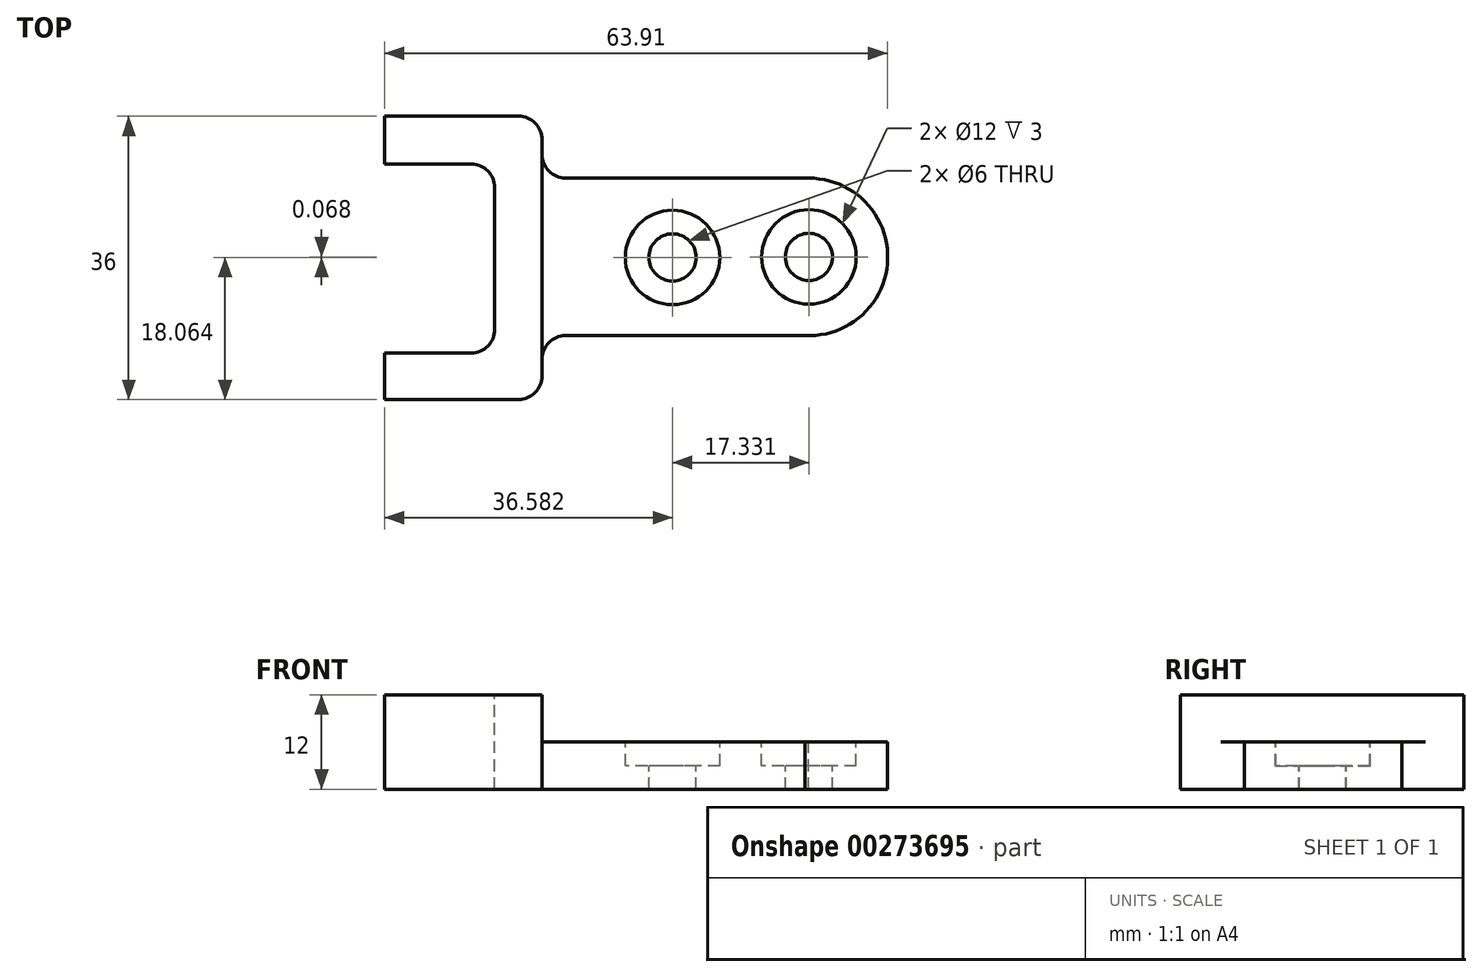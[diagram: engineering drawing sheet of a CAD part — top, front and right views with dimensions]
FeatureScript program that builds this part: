
annotation { "Feature Type Name" : "Feature", "Feature Type Description" : "" }
export const myFeature = defineFeature(function(context is Context, id is Id, definition is map)
    precondition{}
    {
        {
            var Q0;
            Q0=qCreatedBy(makeId("Top.planeOp"),FACE);
            var sketch = newSketch(context, id + "F0", { "sketchPlane" : qUnion([Q0])});
            skLineSegment(sketch, "E0.bottom", {"start": v(-60.7, 27.41) * mm, "end": v(-40.7, 27.41) * mm});
            skLineSegment(sketch, "E0.top", {"start": v(-60.7, -8.59) * mm, "end": v(-40.7, -8.59) * mm});
            skLineSegment(sketch, "E0.left", {"start": v(-60.7, 27.41) * mm, "end": v(-60.7, -8.59) * mm});
            skLineSegment(sketch, "E0.right", {"start": v(-40.7, 27.41) * mm, "end": v(-40.7, -8.59) * mm});
            skSolve(sketch);
        }
        {
            var Q0;
            Q0=makeQuery(id+"F0.imprint","IMPRINT",FACE,{"disambiguationData":[TD([[makeQuery(id+"F0.imprint","IMPRINT",EDGE,{"derivedFrom":sQuery(id+"F0.wireOp",EDGE,"E0.bottom")}),-1.0]])]});
            extrude(context, id + "F1", {"entities" : qUnion([Q0]), "depth" : 12 * mm});
        }
        {
            var Q0;
            Q0=makeQuery(id+"F1.opExtrude","CAP_FACE",FACE,{"disambiguationData":[OSD([sQuery(id+"F0.wireOp",EDGE,"E0.bottom"),sQuery(id+"F0.wireOp",EDGE,"E0.top"),sQuery(id+"F0.wireOp",EDGE,"E0.left"),sQuery(id+"F0.wireOp",EDGE,"E0.right")])],"isStart":false});
            var sketch = newSketch(context, id + "F2", { "sketchPlane" : qUnion([Q0])});
            skLineSegment(sketch, "E1.bottom", {"start": v(-46.7, -2.66) * mm, "end": v(-60.7, -2.66) * mm});
            skLineSegment(sketch, "E1.top", {"start": v(-46.7, 21.34) * mm, "end": v(-60.7, 21.34) * mm});
            skLineSegment(sketch, "E1.left", {"start": v(-46.7, -2.66) * mm, "end": v(-46.7, 21.34) * mm});
            skLineSegment(sketch, "E1.right", {"start": v(-60.7, -2.66) * mm, "end": v(-60.7, 21.34) * mm});
            skSolve(sketch);
        }
        {
            var Q0;
            Q0=makeQuery(id+"F2.imprint","IMPRINT",FACE,{"disambiguationData":[TD([[makeQuery(id+"F2.imprint","IMPRINT",EDGE,{"derivedFrom":sQuery(id+"F2.wireOp",EDGE,"E1.bottom")}),-1.0]])]});
            extrude(context, id + "F3", {"entities" : qUnion([Q0]), "operationType" : NewBodyOperationType.REMOVE, "oppositeDirection" : true, "depth" : 25 * mm});
        }
        {
            var Q0;
            Q0=makeQuery(id+"F1.opExtrude","SWEPT_EDGE",EDGE,{"disambiguationData":[OSD([sQuery(id+"F0.wireOp",EDGE,"E0.top"),sQuery(id+"F0.wireOp",EDGE,"E0.right")])]});
            fillet(context, id + "F4", {"entities" : qUnion([Q0]), "radius" : 3 * mm, "tangentPropagation" : true, "allowEdgeOverflow" : false});
        }
        {
            var Q0;
            Q0=makeQuery(id+"F1.opExtrude","SWEPT_EDGE",EDGE,{"disambiguationData":[OSD([sQuery(id+"F0.wireOp",EDGE,"E0.bottom"),sQuery(id+"F0.wireOp",EDGE,"E0.right")])]});
            var Q1;
            Q1=makeQuery(id+"F3.boolean.opBoolean","COPY",EDGE,{"derivedFrom":makeQuery(id+"F3.opExtrude","SWEPT_EDGE",EDGE,{"disambiguationData":[OSD([sQuery(id+"F2.wireOp",EDGE,"E1.bottom"),sQuery(id+"F2.wireOp",EDGE,"E1.left")])]})});
            var Q2;
            Q2=makeQuery(id+"F3.boolean.opBoolean","COPY",EDGE,{"derivedFrom":makeQuery(id+"F3.opExtrude","SWEPT_EDGE",EDGE,{"disambiguationData":[OSD([sQuery(id+"F2.wireOp",EDGE,"E1.top"),sQuery(id+"F2.wireOp",EDGE,"E1.left")])]})});
            fillet(context, id + "F5", {"entities" : qUnion([Q0, Q1, Q2]), "radius" : 3 * mm, "tangentPropagation" : true, "allowEdgeOverflow" : false});
        }
        {
            var Q0;
            Q0=qCreatedBy(makeId("Top.planeOp"),FACE);
            var sketch = newSketch(context, id + "F6", { "sketchPlane" : qUnion([Q0])});
            skLineSegment(sketch, "E2.bottom", {"start": v(-40.85, -0.44) * mm, "end": v(-6.85, -0.44) * mm});
            skLineSegment(sketch, "E2.top", {"start": v(-40.85, 19.56) * mm, "end": v(-6.85, 19.56) * mm});
            skLineSegment(sketch, "E2.left", {"start": v(-40.85, -0.44) * mm, "end": v(-40.85, 19.56) * mm});
            skLineSegment(sketch, "E2.right", {"start": v(-6.85, -0.44) * mm, "end": v(-6.85, 19.56) * mm});
            skSolve(sketch);
        }
        {
            var Q0;
            Q0=makeQuery(id+"F6.imprint","IMPRINT",FACE,{"disambiguationData":[TD([[makeQuery(id+"F6.imprint","IMPRINT",EDGE,{"derivedFrom":sQuery(id+"F6.wireOp",EDGE,"E2.bottom")}),1.0]])]});
            extrude(context, id + "F7", {"entities" : qUnion([Q0]), "operationType" : NewBodyOperationType.ADD, "depth" : 6 * mm});
        }
        {
            var Q0;
            Q0=makeQuery(id+"F7.boolean.opBoolean","INTERSECT",EDGE,{"derivedFrom":[makeQuery(id+"F1.opExtrude","SWEPT_FACE",FACE,{"disambiguationData":[OSD([sQuery(id+"F0.wireOp",EDGE,"E0.right")])]}),makeQuery(id+"F7.opExtrude","SWEPT_FACE",FACE,{"disambiguationData":[OSD([sQuery(id+"F6.wireOp",EDGE,"E2.top")])]})]});
            fillet(context, id + "F8", {"entities" : qUnion([Q0]), "radius" : 3 * mm, "tangentPropagation" : true, "allowEdgeOverflow" : false});
        }
        {
            var Q0;
            Q0=makeQuery(id+"F7.boolean.opBoolean","INTERSECT",EDGE,{"derivedFrom":[makeQuery(id+"F1.opExtrude","SWEPT_FACE",FACE,{"disambiguationData":[OSD([sQuery(id+"F0.wireOp",EDGE,"E0.right")])]}),makeQuery(id+"F7.opExtrude","SWEPT_FACE",FACE,{"disambiguationData":[OSD([sQuery(id+"F6.wireOp",EDGE,"E2.bottom")])]})]});
            fillet(context, id + "F9", {"entities" : qUnion([Q0]), "radius" : 3 * mm, "tangentPropagation" : true, "allowEdgeOverflow" : false});
        }
        {
            var Q0;
            Q0=makeQuery(id+"F7.opExtrude","CAP_FACE",FACE,{"disambiguationData":[OSD([sQuery(id+"F6.wireOp",EDGE,"E2.bottom"),sQuery(id+"F6.wireOp",EDGE,"E2.top"),sQuery(id+"F6.wireOp",EDGE,"E2.left"),sQuery(id+"F6.wireOp",EDGE,"E2.right")])],"isStart":false});
            var sketch = newSketch(context, id + "F10", { "sketchPlane" : qUnion([Q0])});
            skLineSegment(sketch, "E3", {"start": v(-6.85, 19.56) * mm, "end": v(-6.85, 9.56) * mm});
            skSolve(sketch);
        }
        {
            var Q0;
            {var subQ8=sQuery(id+"F10.wireOp",EDGE,"E3");Q0=makeQuery(id+"F10.imprint","IMPRINT",FACE,{"disambiguationData":[TD([[makeQuery(id+"F10.imprint","IMPRINT",EDGE,{"derivedFrom":subQ8}),1.0]])]});}
            var sketch = newSketch(context, id + "F11", { "sketchPlane" : qUnion([Q0])});
            skCircle(sketch, "E4", {"center": v(-6.8, 9.54) * mm, "radius": 10 * mm});
            skSolve(sketch);
        }
        {
            var Q0;
            {var subQ0=sQuery(id+"F11.wireOp",EDGE,"E4");var subQ1=sQuery(id+"F10.wireOp",EDGE,"E3");var subQ2=makeQuery(id+"F10.imprint","IMPRINT",EDGE,{"derivedFrom":subQ1});var subQ3=makeQuery(id+"F11.imprint","INTERSECT",VERTEX,{"derivedFrom":[subQ2,subQ0]});Q0=makeQuery(id+"F11.imprint","IMPRINT",FACE,{"disambiguationData":[TD([[makeQuery(id+"F11.imprint","IMPRINT",EDGE,{"disambiguationData":[TD([[subQ3,1.0]])],"derivedFrom":subQ0}),1.0]])]});}
            extrude(context, id + "F12", {"entities" : qUnion([Q0]), "operationType" : NewBodyOperationType.ADD, "oppositeDirection" : true, "depth" : 6 * mm});
        }
        {
            var Q0;
            {var subQ0=sQuery(id+"F6.wireOp",EDGE,"E2.right");var subQ1=sQuery(id+"F6.wireOp",EDGE,"E2.bottom");Q0=makeQuery(id+"F12.boolean.opBoolean","MERGE",FACE,{"derivedFrom":[makeQuery(id+"F7.opExtrude","CAP_FACE",FACE,{"disambiguationData":[OSD([subQ1,sQuery(id+"F6.wireOp",EDGE,"E2.top"),sQuery(id+"F6.wireOp",EDGE,"E2.left"),subQ0])],"isStart":false}),makeQuery(id+"F12.opExtrude","CAP_FACE",FACE,{"disambiguationData":[OSD([subQ1,subQ0,sQuery(id+"F10.wireOp",EDGE,"E3"),sQuery(id+"F11.wireOp",EDGE,"E4")])],"isStart":true})]});}
            var sketch = newSketch(context, id + "F13", { "sketchPlane" : qUnion([Q0])});
            skCircle(sketch, "E5", {"center": v(-6.8, 9.54) * mm, "radius": 6 * mm});
            skSolve(sketch);
        }
        {
            var Q0;
            Q0=makeQuery(id+"F13.imprint","IMPRINT",FACE,{"disambiguationData":[TD([[makeQuery(id+"F13.imprint","IMPRINT",EDGE,{"derivedFrom":sQuery(id+"F13.wireOp",EDGE,"E5")}),1.0]])]});
            extrude(context, id + "F14", {"entities" : qUnion([Q0]), "operationType" : NewBodyOperationType.REMOVE, "oppositeDirection" : true, "depth" : 3 * mm});
        }
        {
            var Q0;
            {var subQ0=sQuery(id+"F6.wireOp",EDGE,"E2.right");var subQ1=sQuery(id+"F6.wireOp",EDGE,"E2.bottom");Q0=makeQuery(id+"F12.boolean.opBoolean","MERGE",FACE,{"derivedFrom":[makeQuery(id+"F7.opExtrude","CAP_FACE",FACE,{"disambiguationData":[OSD([subQ1,sQuery(id+"F6.wireOp",EDGE,"E2.top"),sQuery(id+"F6.wireOp",EDGE,"E2.left"),subQ0])],"isStart":false}),makeQuery(id+"F12.opExtrude","CAP_FACE",FACE,{"disambiguationData":[OSD([subQ1,subQ0,sQuery(id+"F10.wireOp",EDGE,"E3"),sQuery(id+"F11.wireOp",EDGE,"E4")])],"isStart":true})]});}
            var sketch = newSketch(context, id + "F15", { "sketchPlane" : qUnion([Q0])});
            skCircle(sketch, "E6", {"center": v(-24.13, 9.47) * mm, "radius": 6 * mm});
            skSolve(sketch);
        }
        {
            var Q0;
            Q0=makeQuery(id+"F15.imprint","IMPRINT",FACE,{"disambiguationData":[TD([[makeQuery(id+"F15.imprint","IMPRINT",EDGE,{"derivedFrom":sQuery(id+"F15.wireOp",EDGE,"E6")}),1.0]])]});
            extrude(context, id + "F16", {"entities" : qUnion([Q0]), "operationType" : NewBodyOperationType.REMOVE, "oppositeDirection" : true, "depth" : 3 * mm});
        }
        {
            var Q0;
            Q0=makeQuery(id+"F16.boolean.opBoolean","COPY",FACE,{"derivedFrom":makeQuery(id+"F16.opExtrude","CAP_FACE",FACE,{"disambiguationData":[OSD([sQuery(id+"F15.wireOp",EDGE,"E6")])],"isStart":false})});
            var sketch = newSketch(context, id + "F17", { "sketchPlane" : qUnion([Q0])});
            skCircle(sketch, "E7", {"center": v(-24.13, 9.47) * mm, "radius": 3 * mm});
            skSolve(sketch);
        }
        {
            var Q0;
            Q0=makeQuery(id+"F17.imprint","IMPRINT",FACE,{"disambiguationData":[TD([[makeQuery(id+"F17.imprint","IMPRINT",EDGE,{"derivedFrom":sQuery(id+"F17.wireOp",EDGE,"E7")}),1.0]])]});
            extrude(context, id + "F18", {"entities" : qUnion([Q0]), "operationType" : NewBodyOperationType.REMOVE, "oppositeDirection" : true, "depth" : 3 * mm});
        }
        {
            var Q0;
            Q0=makeQuery(id+"F14.boolean.opBoolean","COPY",FACE,{"derivedFrom":makeQuery(id+"F14.opExtrude","CAP_FACE",FACE,{"disambiguationData":[OSD([sQuery(id+"F13.wireOp",EDGE,"E5")])],"isStart":false})});
            var sketch = newSketch(context, id + "F19", { "sketchPlane" : qUnion([Q0])});
            skCircle(sketch, "E8", {"center": v(-6.8, 9.54) * mm, "radius": 3 * mm});
            skSolve(sketch);
        }
        {
            var Q0;
            Q0=makeQuery(id+"F19.imprint","IMPRINT",FACE,{"disambiguationData":[TD([[makeQuery(id+"F19.imprint","IMPRINT",EDGE,{"derivedFrom":sQuery(id+"F19.wireOp",EDGE,"E8")}),1.0]])]});
            extrude(context, id + "F20", {"entities" : qUnion([Q0]), "operationType" : NewBodyOperationType.REMOVE, "oppositeDirection" : true, "depth" : 3 * mm});
        }
    });
